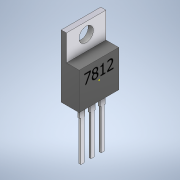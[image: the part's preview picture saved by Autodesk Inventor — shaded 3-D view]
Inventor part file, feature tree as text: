
AUTODESK INVENTOR PART (.ipt)
format: ipt  version: 2020 (Build 240168000, 168)  size: 203,776 bytes
history: native  units: mm
features: sketch x6, projected_geometry x6, extrude x5, other x1
ambient origin geometry x8: Origin, YZ Plane, XZ Plane, XY Plane, X Axis, Y Axis, Z Axis, Center Point
bodies: Body1 (feature_tree)
feature tree (18):
  other  "Sólido1"
  extrude  "Extrusión1"  Depth=9.9mm
  extrude  "Extrusión2"  Depth=2.25mm
  extrude  "Extrusión3"  Depth=1.3mm
  extrude  "Extrusión4"  Depth=6.5mm
  extrude  "Extrusión5"  Depth=3.7mm
  sketch  "Boceto6"  dims[d12=6.5mm d13=0.0mm d14=1.27mm d15=1.27mm d16=1.27mm d17=0.5mm d18=0.5mm d19=0.5mm d20=1.27mm d21=1.27mm d22=4.315mm d23=2.4mm d24=3.0mm d25=0.0mm d26=0.8mm d27=0.8mm d28=0.8mm d29=0.235mm d30=0.235mm d31=0.235mm d32=10.08mm d33=0.0mm]
  sketch  "Boceto1"  dims[d0=4.5mm d1=9.9mm]
  sketch  "Boceto2"  dims[d2=4.95mm d3=2.25mm]
  projected_geometry  "Contorno proyectado1"
  sketch  "Boceto3"  dims[d4=9.2mm d5=0.0mm d6=1.3mm]
  projected_geometry  "Contorno proyectado2"
  sketch  "Boceto4"  dims[d7=6.5mm d8=0.0mm d9=3.6mm]
  projected_geometry  "Contorno proyectado3"
  sketch  "Boceto5"  dims[d10=4.95mm d11=3.7mm]
  projected_geometry  "Contorno proyectado4"
  projected_geometry  "Contorno proyectado5"
  projected_geometry  "Contorno proyectado6"
